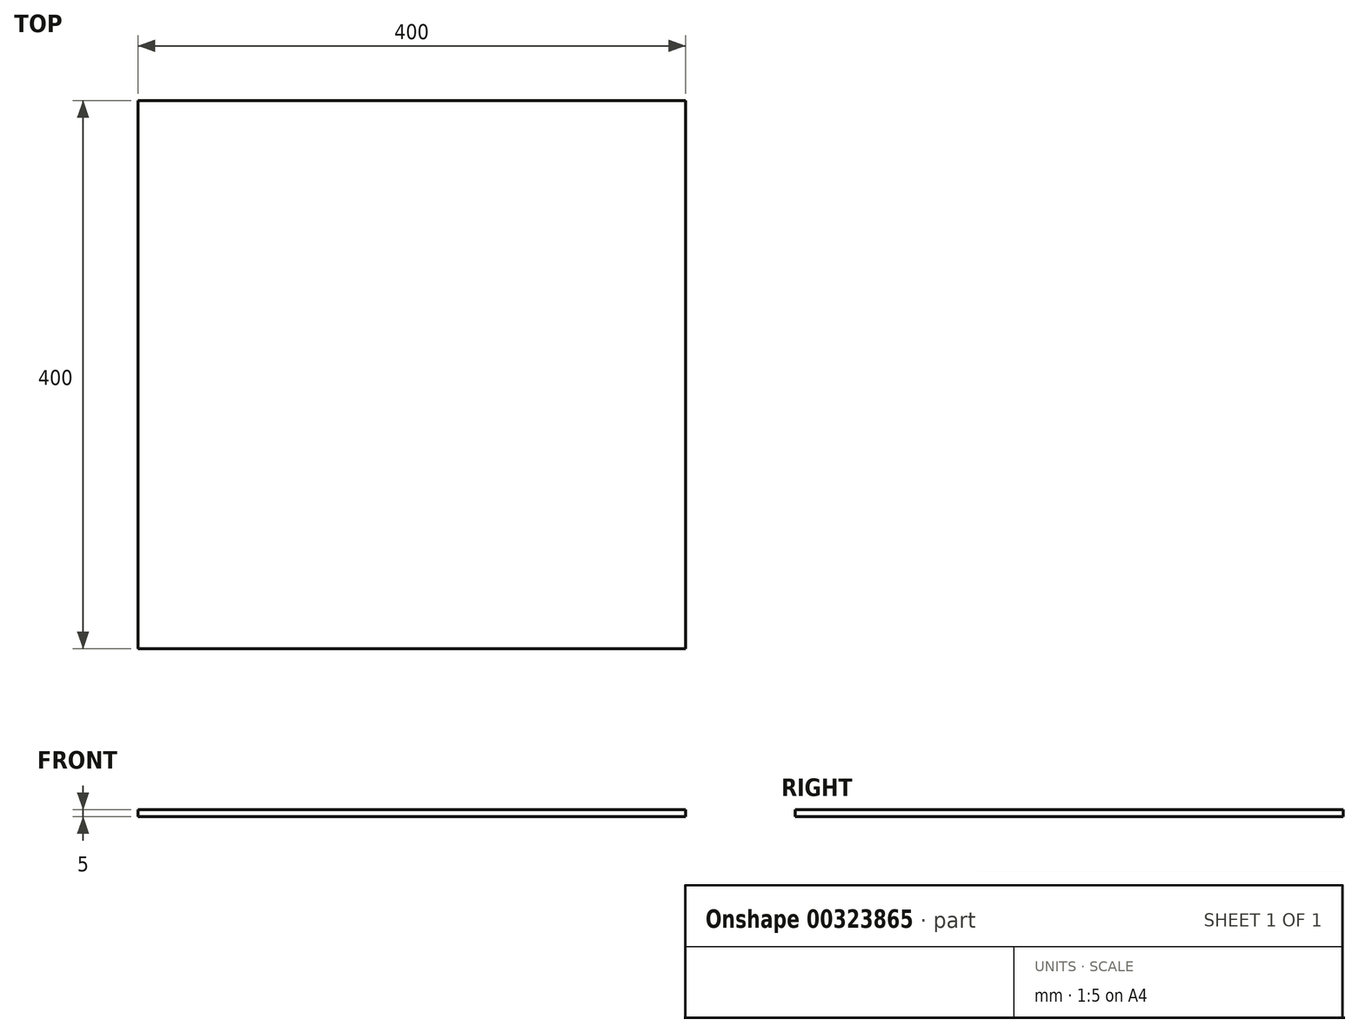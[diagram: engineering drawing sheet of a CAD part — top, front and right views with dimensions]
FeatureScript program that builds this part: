
annotation { "Feature Type Name" : "Feature", "Feature Type Description" : "" }
export const myFeature = defineFeature(function(context is Context, id is Id, definition is map)
    precondition{}
    {
        {
            var Q0;
            Q0=qCreatedBy(makeId("Top.planeOp"),FACE);
            var sketch = newSketch(context, id + "F0", { "sketchPlane" : qUnion([Q0])});
            skLineSegment(sketch, "E0", {"start": v(-200, 0) * mm, "end": v(-200, 200) * mm});
            skLineSegment(sketch, "E1", {"start": v(-200, 0) * mm, "end": v(-200, -200) * mm});
            skLineSegment(sketch, "E2.bottom", {"start": v(-200, 200) * mm, "end": v(200, 200) * mm});
            skLineSegment(sketch, "E2.top", {"start": v(-200, -200) * mm, "end": v(200, -200) * mm});
            skLineSegment(sketch, "E2.left", {"start": v(-200, 200) * mm, "end": v(-200, -200) * mm});
            skLineSegment(sketch, "E2.right", {"start": v(200, 200) * mm, "end": v(200, -200) * mm});
            skLineSegment(sketch, "E3", {"start": v(-200, -200) * mm, "end": v(-200, -70) * mm});
            skLineSegment(sketch, "E4", {"start": v(-200, -70) * mm, "end": v(200, -70) * mm});
            skLineSegment(sketch, "E5", {"start": v(-200, -70) * mm, "end": v(-200, 60) * mm});
            skLineSegment(sketch, "E6", {"start": v(-200, 60) * mm, "end": v(195, 60) * mm});
            skLineSegment(sketch, "E7", {"start": v(195, 60) * mm, "end": v(195, -70) * mm});
            skLineSegment(sketch, "E8", {"start": v(-200, 60) * mm, "end": v(-200, 190) * mm});
            skLineSegment(sketch, "E9", {"start": v(-200, 190) * mm, "end": v(195, 190) * mm});
            skLineSegment(sketch, "E10", {"start": v(195, 190) * mm, "end": v(195, 60) * mm});
            skLineSegment(sketch, "E11", {"start": v(195, 190) * mm, "end": v(65, 190) * mm});
            skLineSegment(sketch, "E12", {"start": v(65, 190) * mm, "end": v(65, 60) * mm});
            skSolve(sketch);
        }
        {
            var Q0;
            {var subQ2=sQuery(id+"F0.wireOp",EDGE,"E2.top");Q0=makeQuery(id+"F0.imprint","IMPRINT",FACE,{"disambiguationData":[TD([[makeQuery(id+"F0.imprint","IMPRINT",EDGE,{"derivedFrom":subQ2}),1.0]])]});}
            extrude(context, id + "F1", {"entities" : qUnion([Q0]), "depth" : 5 * mm});
        }
        {
            var Q0;
            Q0 = qSketchRegion(id + "F0", true);
            extrude(context, id + "F2", {"entities" : qUnion([Q0]), "operationType" : NewBodyOperationType.ADD, "depth" : 5 * mm});
        }
        {
            var Q0;
            {var subQ0=sQuery(id+"F0.wireOp",EDGE,"E10");Q0=makeQuery(id+"F0.imprint","IMPRINT",FACE,{"disambiguationData":[TD([[makeQuery(id+"F0.imprint","IMPRINT",EDGE,{"derivedFrom":subQ0}),-1.0]])]});}
            extrude(context, id + "F3", {"entities" : qUnion([Q0]), "operationType" : NewBodyOperationType.ADD, "depth" : 5 * mm});
        }
    });
